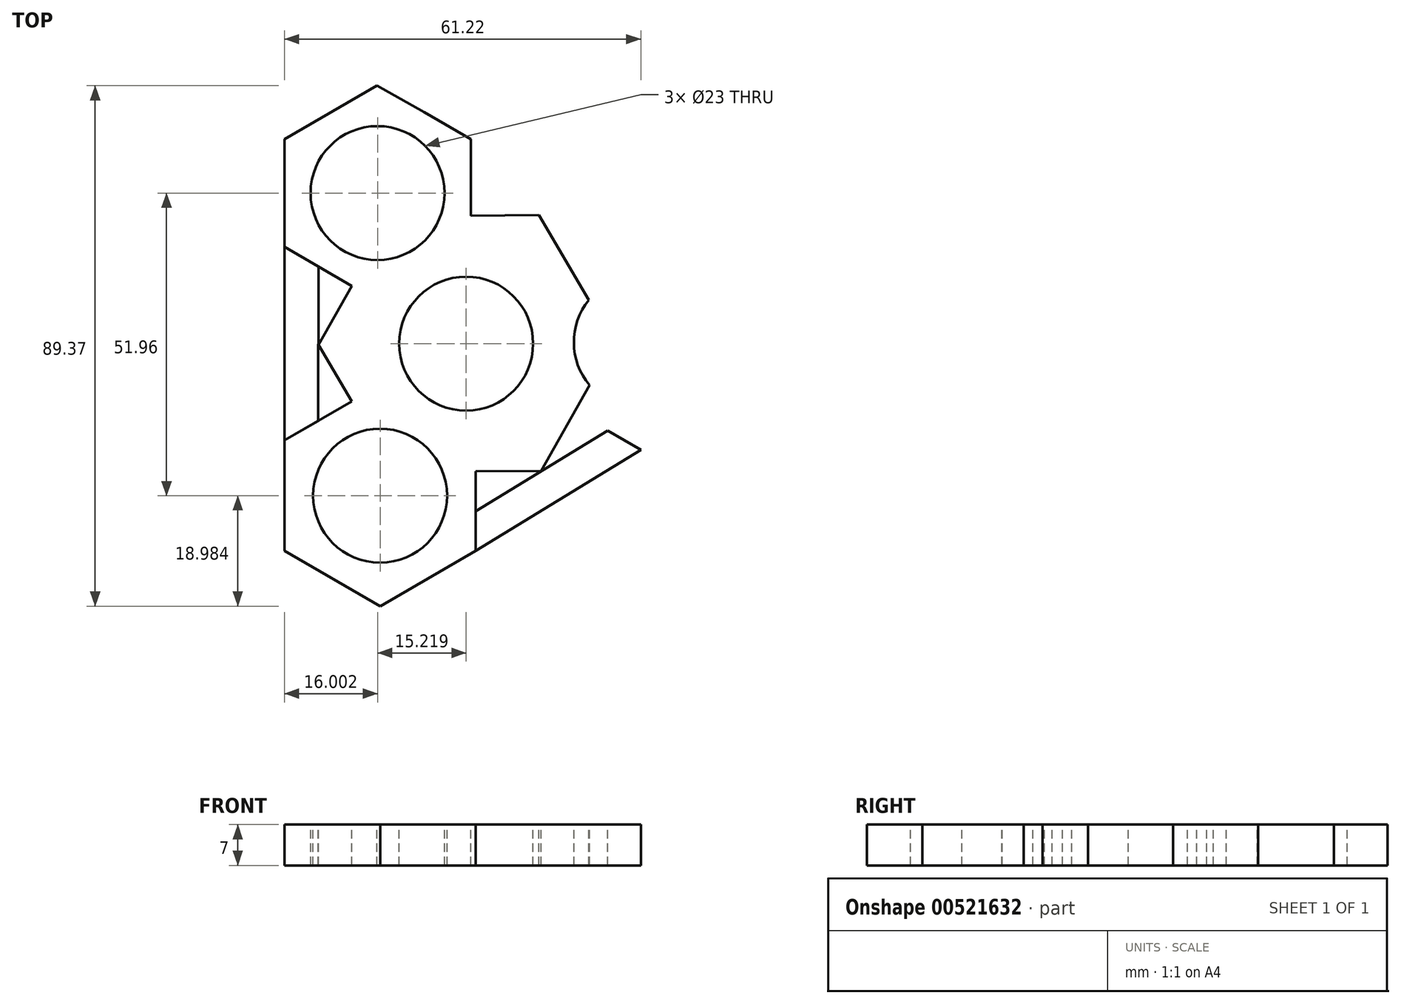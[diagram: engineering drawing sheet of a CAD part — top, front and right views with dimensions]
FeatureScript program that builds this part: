
annotation { "Feature Type Name" : "Feature", "Feature Type Description" : "" }
export const myFeature = defineFeature(function(context is Context, id is Id, definition is map)
    precondition{}
    {
        {
            var Q0;
            Q0=qCreatedBy(makeId("Top.planeOp"),FACE);
            var sketch = newSketch(context, id + "F0", { "sketchPlane" : qUnion([Q0])});
            skCircle(sketch, "E0", {"center": v(0, 0) * mm, "radius": 11.5 * mm});
            skCircle(sketch, "E1", {"center": v(-15.22, 25.85) * mm, "radius": 11.5 * mm});
            skCircle(sketch, "E2", {"center": v(-14.78, -26.1) * mm, "radius": 11.5 * mm});
            skCircle(sketch, "E3", {"center": v(30, 0.25) * mm, "radius": 11.5 * mm});
            skPoint(sketch, "E4.0.midPoint", {"position": v(5.37, -17.18) * mm});
            skPoint(sketch, "E5.0.midPoint", {"position": v(-24.47, 12.8) * mm});
            skPoint(sketch, "E6.0.midPoint", {"position": v(-5.82, -12.85) * mm});
            skLineSegment(sketch, "E7.2", {"start": v(30, 18.73) * mm, "end": v(46, 9.5) * mm});
            skPoint(sketch, "E7.0.midPoint", {"position": v(14, 0.25) * mm});
            skLineSegment(sketch, "E8.4", {"start": v(-15.37, 44.33) * mm, "end": v(0.7, 35.23) * mm});
            skPoint(sketch, "E8.0.midPoint", {"position": v(-7.1, 12.06) * mm});
            skPoint(sketch, "E9.0.midPoint", {"position": v(-15.06, 7.38) * mm});
            skCircle(sketch, "E10.cCircle", {"center": v(0, 0) * mm, "radius": 21.95 * mm, "construction": true});
            skLineSegment(sketch, "E10.0", {"start": v(-12.86, 21.85) * mm, "end": v(12.49, 22.06) * mm});
            skLineSegment(sketch, "E10.1", {"start": v(12.49, 22.06) * mm, "end": v(25.35, 0.21) * mm});
            skLineSegment(sketch, "E10.2", {"start": v(25.35, 0.21) * mm, "end": v(12.86, -21.85) * mm});
            skLineSegment(sketch, "E10.3", {"start": v(12.86, -21.85) * mm, "end": v(-12.49, -22.06) * mm});
            skLineSegment(sketch, "E10.4", {"start": v(-12.49, -22.06) * mm, "end": v(-25.35, -0.21) * mm});
            skLineSegment(sketch, "E10.5", {"start": v(-25.35, -0.21) * mm, "end": v(-12.86, 21.85) * mm});
            skPoint(sketch, "E10.0.midPoint", {"position": v(-0.19, 21.95) * mm});
            skLineSegment(sketch, "E11", {"start": v(30, 18.73) * mm, "end": v(0.7, 35.23) * mm});
            skCircle(sketch, "E12.cCircle", {"center": v(30, 0.25) * mm, "radius": 16 * mm, "construction": true});
            skLineSegment(sketch, "E12.1", {"start": v(46, 9.5) * mm, "end": v(46, -8.98) * mm});
            skLineSegment(sketch, "E12.2", {"start": v(46, -8.98) * mm, "end": v(30, -18.22) * mm});
            skLineSegment(sketch, "E12.3", {"start": v(30, -18.22) * mm, "end": v(14, -8.98) * mm});
            skLineSegment(sketch, "E12.5", {"start": v(14, 9.5) * mm, "end": v(30, 18.73) * mm});
            skPoint(sketch, "E12.0.midPoint", {"position": v(38, 14.1) * mm});
            skPoint(sketch, "E13.0.midPoint", {"position": v(-9.03, -36.07) * mm});
            skCircle(sketch, "E14.cCircle", {"center": v(-15.22, 25.85) * mm, "radius": 16 * mm, "construction": true});
            skLineSegment(sketch, "E14.0", {"start": v(-15.22, 44.33) * mm, "end": v(0.78, 35.1) * mm});
            skLineSegment(sketch, "E14.1", {"start": v(0.78, 35.1) * mm, "end": v(0.78, 16.62) * mm});
            skLineSegment(sketch, "E14.3", {"start": v(-15.22, 7.38) * mm, "end": v(-31.22, 16.62) * mm});
            skLineSegment(sketch, "E14.4", {"start": v(-31.22, 16.62) * mm, "end": v(-31.22, 35.1) * mm});
            skLineSegment(sketch, "E14.5", {"start": v(-31.22, 35.1) * mm, "end": v(-15.22, 44.33) * mm});
            skPoint(sketch, "E14.0.midPoint", {"position": v(-7.22, 39.71) * mm});
            skCircle(sketch, "E15.cCircle", {"center": v(-14.78, -26.1) * mm, "radius": 16.44 * mm, "construction": true});
            skPoint(sketch, "E15.cCircle.perimeterSnap0", {"position": v(-31.22, -27.8) * mm});
            skLineSegment(sketch, "E15.0", {"start": v(-31.22, -35.6) * mm, "end": v(-31.22, -16.62) * mm});
            skLineSegment(sketch, "E15.1", {"start": v(-31.22, -16.62) * mm, "end": v(-14.78, -7.12) * mm});
            skLineSegment(sketch, "E15.3", {"start": v(1.66, -16.62) * mm, "end": v(1.66, -35.6) * mm});
            skLineSegment(sketch, "E15.4", {"start": v(1.66, -35.6) * mm, "end": v(-14.78, -45.09) * mm});
            skLineSegment(sketch, "E15.5", {"start": v(-14.78, -45.09) * mm, "end": v(-31.22, -35.6) * mm});
            skPoint(sketch, "E15.0.midPoint", {"position": v(-31.22, -26.1) * mm});
            skPoint(sketch, "E15.0.midPoint.positionSnap0", {"position": v(-31.22, -27.8) * mm});
            skLineSegment(sketch, "E16", {"start": v(-31.22, 16.62) * mm, "end": v(-31.22, -16.62) * mm});
            skLineSegment(sketch, "E17", {"start": v(1.66, -35.6) * mm, "end": v(30, -18.22) * mm});
            skLineSegment(sketch, "E18", {"start": v(-25.35, -0.21) * mm, "end": v(-24.47, 12.8) * mm});
            skLineSegment(sketch, "E19", {"start": v(-25.35, -0.21) * mm, "end": v(-25.35, -13.23) * mm});
            skLineSegment(sketch, "E20", {"start": v(12.49, 22.06) * mm, "end": v(0.78, 28.69) * mm});
            skLineSegment(sketch, "E21", {"start": v(12.49, 22.06) * mm, "end": v(24.48, 15.27) * mm});
            skLineSegment(sketch, "E22", {"start": v(12.86, -21.85) * mm, "end": v(24.22, -14.88) * mm});
            skLineSegment(sketch, "E23", {"start": v(12.86, -21.85) * mm, "end": v(1.43, -28.85) * mm});
            skSolve(sketch);
        }
        {
            var Q0;
            Q0=makeQuery(id+"F0.imprint","IMPRINT",FACE,{"disambiguationData":[TD([[makeQuery(id+"F0.imprint","IMPRINT",EDGE,{"derivedFrom":sQuery(id+"F0.wireOp",EDGE,"E0")}),-1.0]])]});
            var Q1;
            {var subQ0=sQuery(id+"F0.wireOp",EDGE,"E14.4");Q1=makeQuery(id+"F0.imprint","IMPRINT",FACE,{"disambiguationData":[TD([[makeQuery(id+"F0.imprint","IMPRINT",EDGE,{"derivedFrom":subQ0}),-1.0]])]});}
            var Q2;
            {var subQ0=sQuery(id+"F0.wireOp",EDGE,"E7.2");Q2=makeQuery(id+"F0.imprint","IMPRINT",FACE,{"disambiguationData":[TD([[makeQuery(id+"F0.imprint","IMPRINT",EDGE,{"derivedFrom":subQ0}),-1.0]])]});}
            var Q3;
            {var subQ5=sQuery(id+"F0.wireOp",EDGE,"E15.0");Q3=makeQuery(id+"F0.imprint","IMPRINT",FACE,{"disambiguationData":[TD([[makeQuery(id+"F0.imprint","IMPRINT",EDGE,{"derivedFrom":subQ5}),-1.0]])]});}
            extrude(context, id + "F1", {"entities" : qUnion([Q0, Q1, Q2, Q3]), "oppositeDirection" : true, "depth" : 7 * mm, "offsetDistance" : 25 * mm});
        }
        {
            var Q0;
            Q0=makeQuery(id+"F1.opExtrude","CAP_FACE",FACE,{"disambiguationData":[OSD([sQuery(id+"F0.wireOp",EDGE,"E0"),sQuery(id+"F0.wireOp",EDGE,"E1"),sQuery(id+"F0.wireOp",EDGE,"E2"),sQuery(id+"F0.wireOp",EDGE,"E3"),sQuery(id+"F0.wireOp",EDGE,"E8.4"),sQuery(id+"F0.wireOp",EDGE,"E10.0"),sQuery(id+"F0.wireOp",EDGE,"E10.1"),sQuery(id+"F0.wireOp",EDGE,"E10.2"),sQuery(id+"F0.wireOp",EDGE,"E10.3"),sQuery(id+"F0.wireOp",EDGE,"E10.4"),sQuery(id+"F0.wireOp",EDGE,"E10.5"),sQuery(id+"F0.wireOp",EDGE,"E7.2"),sQuery(id+"F0.wireOp",EDGE,"E12.1"),sQuery(id+"F0.wireOp",EDGE,"E12.2"),sQuery(id+"F0.wireOp",EDGE,"E12.3"),sQuery(id+"F0.wireOp",EDGE,"E12.5"),sQuery(id+"F0.wireOp",EDGE,"E14.0"),sQuery(id+"F0.wireOp",EDGE,"E14.1"),sQuery(id+"F0.wireOp",EDGE,"E14.3"),sQuery(id+"F0.wireOp",EDGE,"E14.4"),sQuery(id+"F0.wireOp",EDGE,"E14.5"),sQuery(id+"F0.wireOp",EDGE,"E15.0"),sQuery(id+"F0.wireOp",EDGE,"E15.1"),sQuery(id+"F0.wireOp",EDGE,"E15.3"),sQuery(id+"F0.wireOp",EDGE,"E15.4"),sQuery(id+"F0.wireOp",EDGE,"E15.5")])],"isStart":true});
            var sketch = newSketch(context, id + "F2", { "sketchPlane" : qUnion([Q0])});
            skLineSegment(sketch, "E24", {"start": v(1.66, -35.6) * mm, "end": v(30, -18.22) * mm});
            skLineSegment(sketch, "E25", {"start": v(30, -18.22) * mm, "end": v(24.31, -14.94) * mm});
            skLineSegment(sketch, "E26", {"start": v(24.31, -14.94) * mm, "end": v(1.66, -28.77) * mm});
            skLineSegment(sketch, "E27", {"start": v(30, 18.73) * mm, "end": v(0.78, 35.1) * mm});
            skLineSegment(sketch, "E28", {"start": v(0.78, 35.1) * mm, "end": v(0.78, 28.53) * mm});
            skLineSegment(sketch, "E29", {"start": v(0.78, 28.53) * mm, "end": v(24.2, 15.38) * mm});
            skLineSegment(sketch, "E30", {"start": v(-31.22, 16.62) * mm, "end": v(-31.22, -16.62) * mm});
            skLineSegment(sketch, "E31", {"start": v(-31.22, -16.62) * mm, "end": v(-25.43, -13.27) * mm});
            skLineSegment(sketch, "E32", {"start": v(-25.43, -13.27) * mm, "end": v(-25.35, 13.23) * mm});
            skSolve(sketch);
        }
        {
            var Q0;
            {var subQ0=sQuery(id+"F2.wireOp",EDGE,"E30");Q0=makeQuery(id+"F2.imprint","IMPRINT",FACE,{"disambiguationData":[TD([[makeQuery(id+"F2.imprint","IMPRINT",EDGE,{"derivedFrom":subQ0}),1.0]])]});}
            var Q1;
            {var subQ8=sQuery(id+"F2.wireOp",EDGE,"E27");Q1=makeQuery(id+"F2.imprint","IMPRINT",FACE,{"disambiguationData":[TD([[makeQuery(id+"F2.imprint","IMPRINT",EDGE,{"derivedFrom":subQ8}),1.0]])]});}
            var Q2;
            {var subQ0=sQuery(id+"F2.wireOp",EDGE,"E24");Q2=makeQuery(id+"F2.imprint","IMPRINT",FACE,{"disambiguationData":[TD([[makeQuery(id+"F2.imprint","IMPRINT",EDGE,{"derivedFrom":subQ0}),1.0]])]});}
            extrude(context, id + "F3", {"entities" : qUnion([Q0, Q1, Q2]), "oppositeDirection" : true, "depth" : 7 * mm, "offsetDistance" : 25 * mm});
        }
    });
